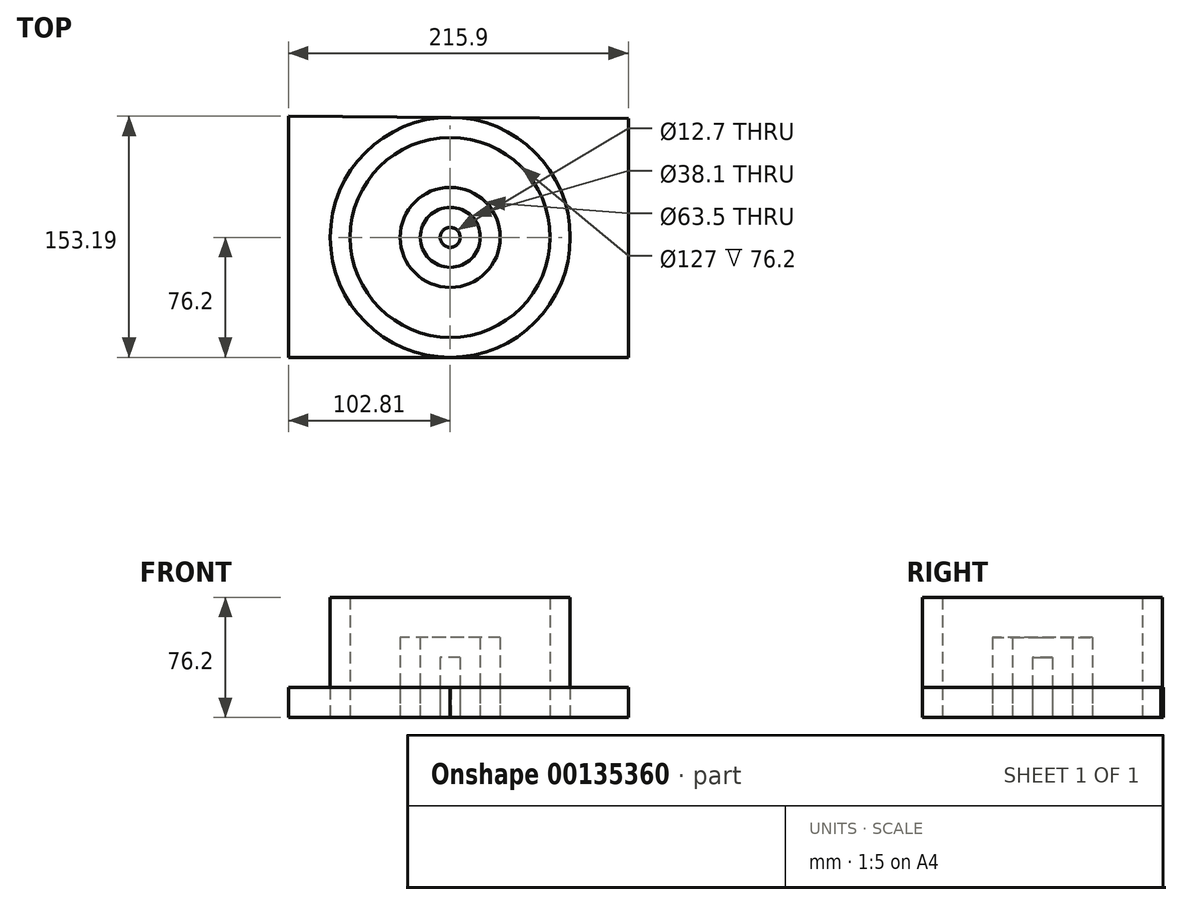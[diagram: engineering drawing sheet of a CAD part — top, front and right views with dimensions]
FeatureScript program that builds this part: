
annotation { "Feature Type Name" : "Feature", "Feature Type Description" : "" }
export const myFeature = defineFeature(function(context is Context, id is Id, definition is map)
    precondition{}
    {
        {
            var Q0;
            Q0=qCreatedBy(makeId("Top.planeOp"),FACE);
            var sketch = newSketch(context, id + "F0", { "sketchPlane" : qUnion([Q0])});
            skCircle(sketch, "E0", {"center": v(0, 0) * mm, "radius": 19.05 * mm});
            skCircle(sketch, "E1", {"center": v(0, 0) * mm, "radius": 63.5 * mm});
            skCircle(sketch, "E2", {"center": v(0, 0) * mm, "radius": 76.2 * mm});
            skCircle(sketch, "E3", {"center": v(0, 0) * mm, "radius": 6.35 * mm});
            skCircle(sketch, "E4", {"center": v(0, 0) * mm, "radius": 31.75 * mm});
            skLineSegment(sketch, "E5", {"start": v(113.09, 75.33) * mm, "end": v(113.09, -76.2) * mm});
            skLineSegment(sketch, "E6", {"start": v(113.09, -76.2) * mm, "end": v(-102.81, -76.2) * mm});
            skLineSegment(sketch, "E7", {"start": v(-102.81, -76.2) * mm, "end": v(-102.81, 77) * mm});
            skLineSegment(sketch, "E8", {"start": v(-102.81, 77) * mm, "end": v(113.09, 75.33) * mm});
            skSolve(sketch);
        }
        {
            var Q0;
            Q0=makeQuery(id+"F0.imprint","IMPRINT",FACE,{"disambiguationData":[TD([[makeQuery(id+"F0.imprint","IMPRINT",EDGE,{"derivedFrom":sQuery(id+"F0.wireOp",EDGE,"E1")}),-1.0]])]});
            extrude(context, id + "F1", {"entities" : qUnion([Q0]), "depth" : 76.2 * mm});
        }
        {
            var Q0;
            Q0=makeQuery(id+"F0.imprint","IMPRINT",FACE,{"disambiguationData":[TD([[makeQuery(id+"F0.imprint","IMPRINT",EDGE,{"derivedFrom":sQuery(id+"F0.wireOp",EDGE,"E0")}),-1.0]])]});
            extrude(context, id + "F2", {"entities" : qUnion([Q0]), "depth" : 50.8 * mm});
        }
        {
            var Q0;
            Q0=makeQuery(id+"F0.imprint","IMPRINT",FACE,{"disambiguationData":[TD([[makeQuery(id+"F0.imprint","IMPRINT",EDGE,{"derivedFrom":sQuery(id+"F0.wireOp",EDGE,"E3")}),1.0]])]});
            extrude(context, id + "F3", {"entities" : qUnion([Q0]), "depth" : 38.1 * mm});
        }
        {
            var Q0;
            {var subQ5=sQuery(id+"F0.wireOp",EDGE,"E7");Q0=makeQuery(id+"F0.imprint","IMPRINT",FACE,{"disambiguationData":[TD([[makeQuery(id+"F0.imprint","IMPRINT",EDGE,{"derivedFrom":subQ5}),-1.0]])]});}
            var Q1;
            {var subQ5=sQuery(id+"F0.wireOp",EDGE,"E5");Q1=makeQuery(id+"F0.imprint","IMPRINT",FACE,{"disambiguationData":[TD([[makeQuery(id+"F0.imprint","IMPRINT",EDGE,{"derivedFrom":subQ5}),-1.0]])]});}
            var Q2;
            Q2=makeQuery(id+"F0.imprint","IMPRINT",FACE,{"disambiguationData":[TD([[makeQuery(id+"F0.imprint","IMPRINT",EDGE,{"derivedFrom":sQuery(id+"F0.wireOp",EDGE,"E1")}),1.0]])]});
            var Q3;
            Q3=makeQuery(id+"F0.imprint","IMPRINT",FACE,{"disambiguationData":[TD([[makeQuery(id+"F0.imprint","IMPRINT",EDGE,{"derivedFrom":sQuery(id+"F0.wireOp",EDGE,"E0")}),1.0]])]});
            extrude(context, id + "F4", {"entities" : qUnion([Q0, Q1, Q2, Q3]), "depth" : 19.05 * mm});
        }
    });
